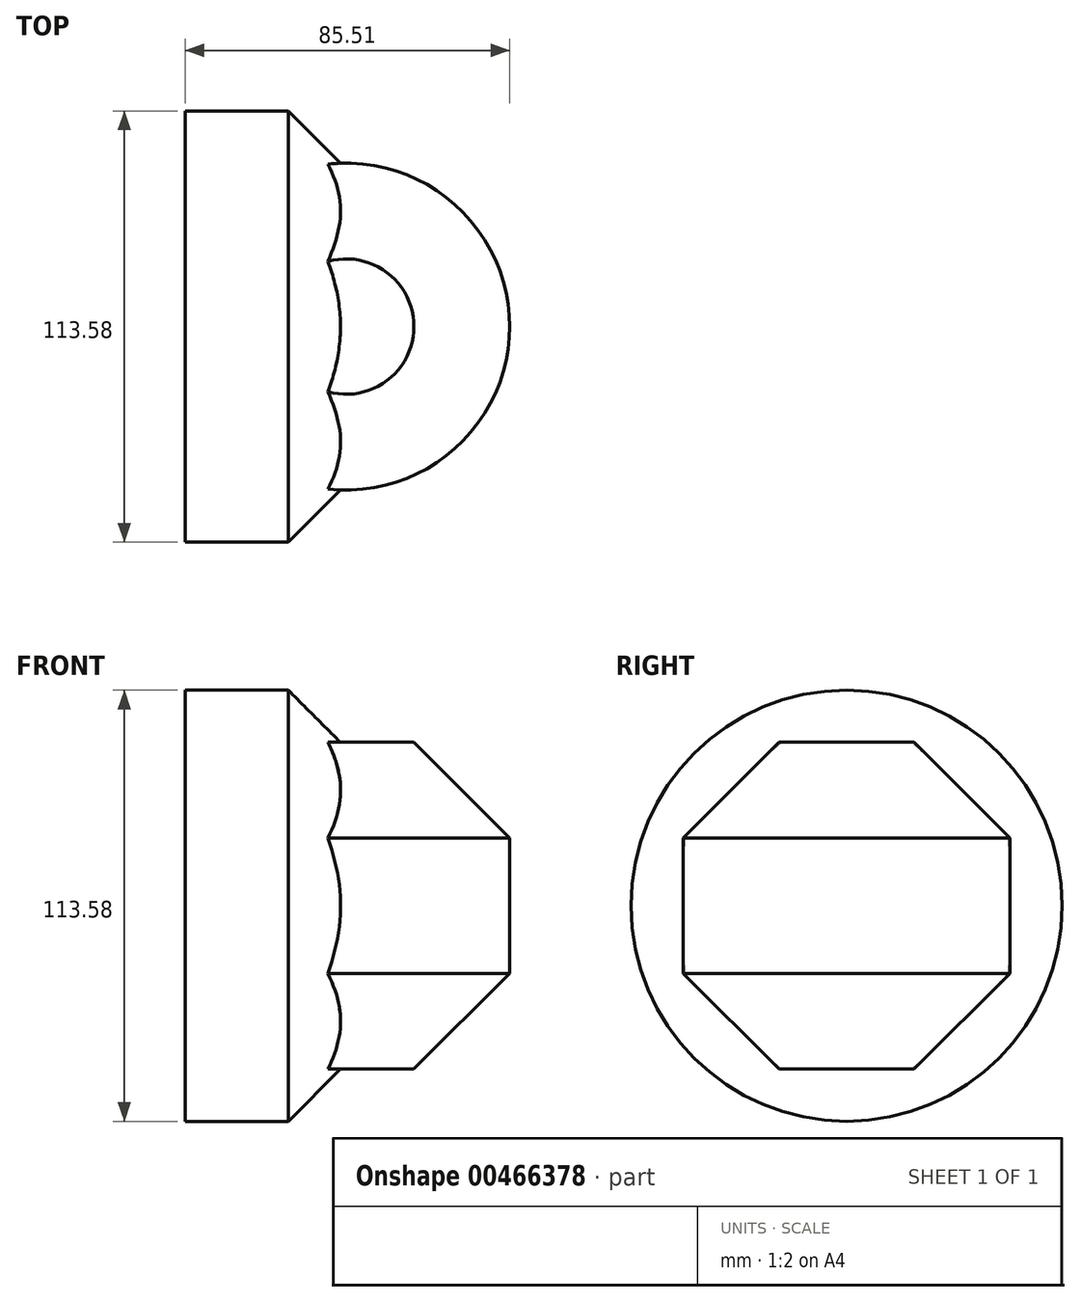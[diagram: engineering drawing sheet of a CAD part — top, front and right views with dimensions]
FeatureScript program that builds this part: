
annotation { "Feature Type Name" : "Feature", "Feature Type Description" : "" }
export const myFeature = defineFeature(function(context is Context, id is Id, definition is map)
    precondition{}
    {
        {
            var Q0;
            Q0=qCreatedBy(makeId("Front.planeOp"),FACE);
            var sketch = newSketch(context, id + "F0", { "sketchPlane" : qUnion([Q0])});
            skLineSegment(sketch, "E0", {"start": v(0, 0) * mm, "end": v(0, 56.6) * mm});
            skLineSegment(sketch, "E1.bottom", {"start": v(-42.45, 56.79) * mm, "end": v(-13.6, 56.79) * mm});
            skLineSegment(sketch, "E1.top", {"start": v(-42.45, 0) * mm, "end": v(-13.6, 0) * mm});
            skLineSegment(sketch, "E1.left", {"start": v(-42.45, 56.79) * mm, "end": v(-42.45, 0) * mm});
            skLineSegment(sketch, "E2", {"start": v(-13.6, 0) * mm, "end": v(0, 0) * mm});
            skLineSegment(sketch, "E3", {"start": v(-13.6, 56.79) * mm, "end": v(0, 56.6) * mm});
            skSolve(sketch);
        }
        {
            var Q0;
            Q0=makeQuery(id+"F0.imprint","IMPRINT",FACE,{"disambiguationData":[TD([[makeQuery(id+"F0.imprint","IMPRINT",EDGE,{"derivedFrom":sQuery(id+"F0.wireOp",EDGE,"E1.right")}),1.0]])]});
            var Q1;
            Q1=makeQuery(id+"F0.imprint","IMPRINT",FACE,{"disambiguationData":[TD([[makeQuery(id+"F0.imprint","IMPRINT",EDGE,{"derivedFrom":sQuery(id+"F0.wireOp",EDGE,"E1.bottom")}),-1.0]])]});
            var Q2;
            Q2=sQuery(id+"F0.wireOp",EDGE,"E1.top");
            revolve(context, id + "F1", {"entities" : qUnion([Q0, Q1]), "axis" : qUnion([Q2]), "revolveType" : RevolveType.FULL});
        }
        {
            var Q0;
            Q0=qCreatedBy(makeId("Front.planeOp"),FACE);
            var sketch = newSketch(context, id + "F2", { "sketchPlane" : qUnion([Q0])});
            skLineSegment(sketch, "E4.2", {"start": v(0, 43.06) * mm, "end": v(17.83, 43.06) * mm});
            skLineSegment(sketch, "E4.3", {"start": v(17.83, 43.06) * mm, "end": v(43.06, 17.83) * mm});
            skLineSegment(sketch, "E4.4", {"start": v(43.06, 17.83) * mm, "end": v(43.06, -17.83) * mm});
            skLineSegment(sketch, "E4.5", {"start": v(43.06, -17.83) * mm, "end": v(17.83, -43.06) * mm});
            skLineSegment(sketch, "E4.6", {"start": v(17.83, -43.06) * mm, "end": v(0, -43.06) * mm});
            skPoint(sketch, "E4.0.midPoint", {"position": v(-43.06, 0) * mm});
            skPoint(sketch, "E5.orphan", {"position": v(-17.83, 43.06) * mm});
            skPoint(sketch, "E6.orphan", {"position": v(-17.83, -43.06) * mm});
            skArc(sketch, "E7.trimOffspring", {"start": v(0, -43.06) * mm, "mid": v(43.06, 0) * mm, "end": v(0, 43.06) * mm, "construction": true});
            skPoint(sketch, "E8.orphan", {"position": v(-43.06, -17.83) * mm});
            skPoint(sketch, "E4.1.start.orphan", {"position": v(-43.06, 17.83) * mm});
            skLineSegment(sketch, "E9", {"start": v(0, -43.06) * mm, "end": v(0, 43.06) * mm});
            skSolve(sketch);
        }
        {
            var Q0;
            Q0=makeQuery(id+"F2.imprint","IMPRINT",FACE,{"disambiguationData":[TD([[makeQuery(id+"F2.imprint","IMPRINT",EDGE,{"derivedFrom":sQuery(id+"F2.wireOp",EDGE,"E4.2")}),-1.0]])]});
            var Q1;
            Q1=sQuery(id+"F2.wireOp",EDGE,"E9");
            revolve(context, id + "F3", {"operationType" : NewBodyOperationType.ADD, "entities" : qUnion([Q0]), "axis" : qUnion([Q1]), "revolveType" : RevolveType.SYMMETRIC, "angle" : 180 * degree});
        }
        {
            var Q0;
            Q0=makeQuery(id+"F1.opRevolve","SWEPT_EDGE",EDGE,{"disambiguationData":[OSD([sQuery(id+"F0.wireOp",EDGE,"E0"),sQuery(id+"F0.wireOp",EDGE,"E3")])]});
            chamfer(context, id + "F4", {"entities" : qUnion([Q0]), "width" : 15.24 * mm, "tangentPropagation" : true});
        }
    });
